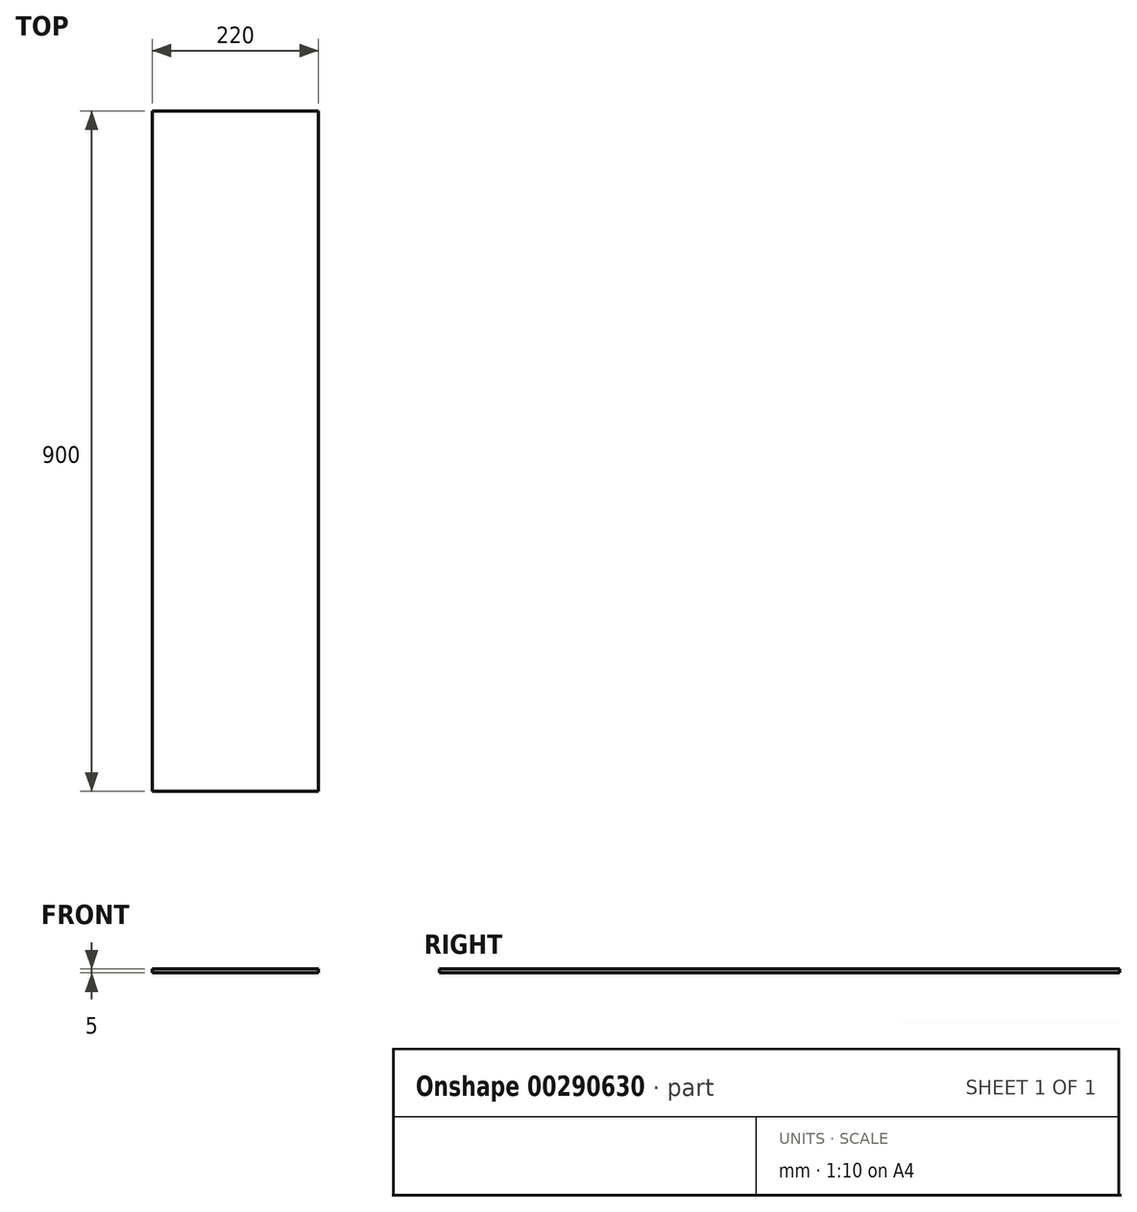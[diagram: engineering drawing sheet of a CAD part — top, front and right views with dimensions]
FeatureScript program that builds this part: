
annotation { "Feature Type Name" : "Feature", "Feature Type Description" : "" }
export const myFeature = defineFeature(function(context is Context, id is Id, definition is map)
    precondition{}
    {
        {
            var Q0;
            Q0=qCreatedBy(makeId("Top.planeOp"),FACE);
            var sketch = newSketch(context, id + "F0", { "sketchPlane" : qUnion([Q0])});
            skLineSegment(sketch, "E0.bottom", {"start": v(-110, 450) * mm, "end": v(110, 450) * mm});
            skLineSegment(sketch, "E0.top", {"start": v(-110, -450) * mm, "end": v(110, -450) * mm});
            skLineSegment(sketch, "E0.left", {"start": v(-110, 450) * mm, "end": v(-110, -450) * mm});
            skLineSegment(sketch, "E0.right", {"start": v(110, 450) * mm, "end": v(110, -450) * mm});
            skLineSegment(sketch, "E1", {"start": v(-110, 0) * mm, "end": v(110, 0) * mm, "construction": true});
            skLineSegment(sketch, "E2", {"start": v(0, 450) * mm, "end": v(0, -450) * mm, "construction": true});
            skLineSegment(sketch, "E3", {"start": v(-110, 400) * mm, "end": v(110, 400) * mm, "construction": true});
            skLineSegment(sketch, "E4.MirrorCS", {"start": v(-110, -400) * mm, "end": v(110, -400) * mm, "construction": true});
            skLineSegment(sketch, "E5", {"start": v(-125, 450) * mm, "end": v(-125, 400) * mm, "construction": true});
            skLineSegment(sketch, "E6.MirrorCS", {"start": v(125, 450) * mm, "end": v(125, 400) * mm, "construction": true});
            skLineSegment(sketch, "E7.MirrorCS", {"start": v(-125, -450) * mm, "end": v(-125, -400) * mm, "construction": true});
            skLineSegment(sketch, "E8.MirrorCS", {"start": v(125, -450) * mm, "end": v(125, -400) * mm, "construction": true});
            skLineSegment(sketch, "E9", {"start": v(-110, 400) * mm, "end": v(-125, 400) * mm});
            skLineSegment(sketch, "E10", {"start": v(-110, 437.5) * mm, "end": v(110, 437.5) * mm, "construction": true});
            skLineSegment(sketch, "E11", {"start": v(-90, 450) * mm, "end": v(-90, 437.5) * mm, "construction": true});
            skLineSegment(sketch, "E12.MirrorCS", {"start": v(90, 450) * mm, "end": v(90, 437.5) * mm, "construction": true});
            skLineSegment(sketch, "E13.MirrorCS", {"start": v(-110, -437.5) * mm, "end": v(110, -437.5) * mm, "construction": true});
            skLineSegment(sketch, "E14.MirrorCS", {"start": v(-90, -450) * mm, "end": v(-90, -437.5) * mm, "construction": true});
            skLineSegment(sketch, "E15.MirrorCS", {"start": v(90, -450) * mm, "end": v(90, -437.5) * mm, "construction": true});
            skSolve(sketch);
        }
        {
            var Q0;
            Q0 = qSketchRegion(id + "F0", true);
            extrude(context, id + "F1", {"entities" : qUnion([Q0]), "depth" : 5 * mm});
        }
    });
